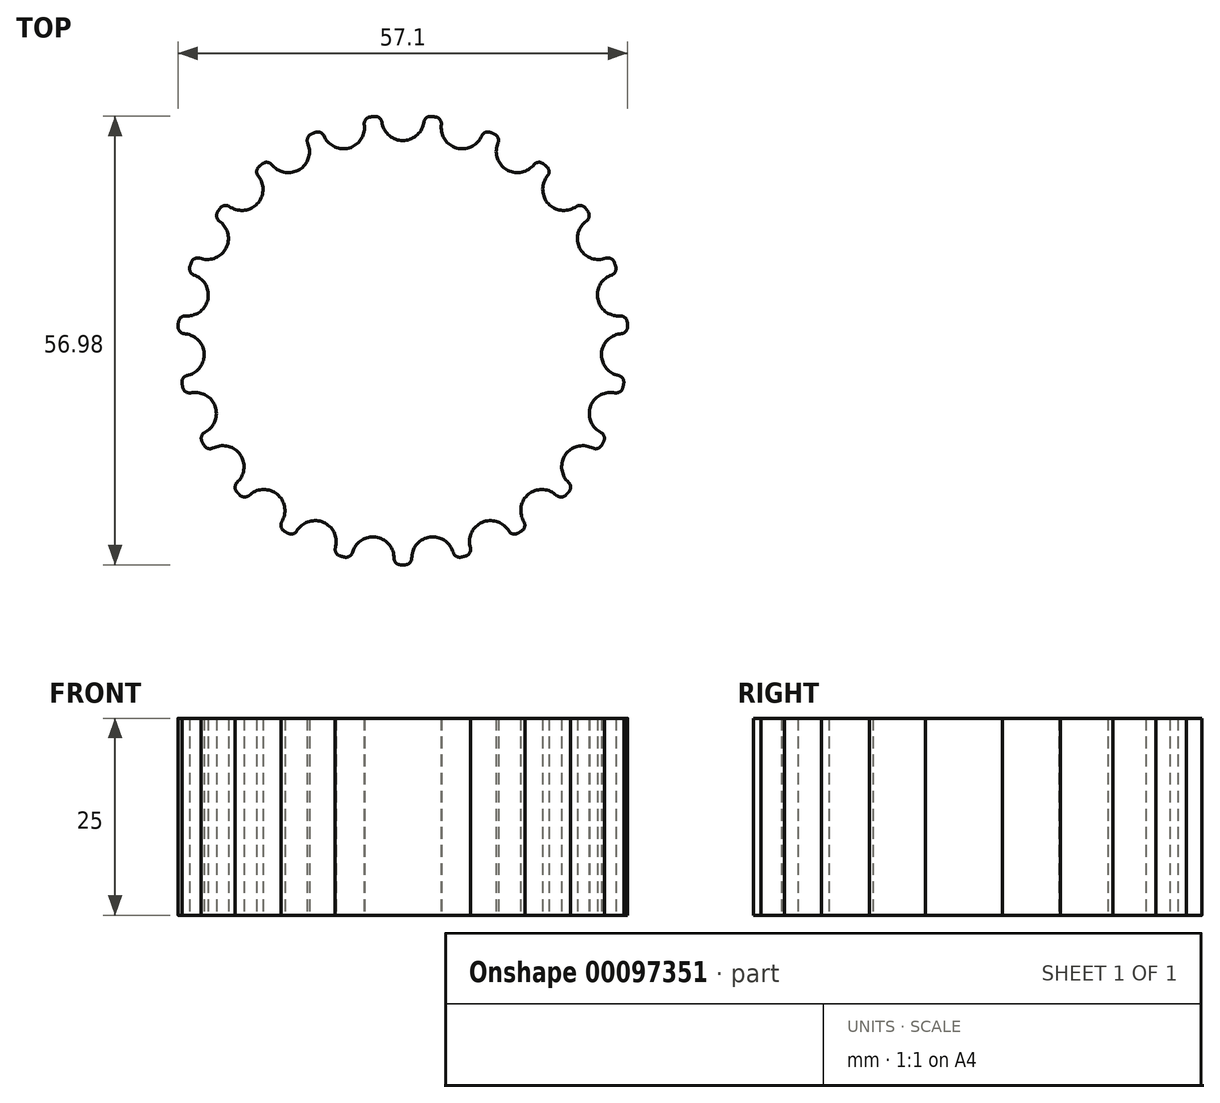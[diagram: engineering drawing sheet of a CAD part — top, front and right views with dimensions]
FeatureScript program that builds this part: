
annotation { "Feature Type Name" : "Feature", "Feature Type Description" : "" }
export const myFeature = defineFeature(function(context is Context, id is Id, definition is map)
    precondition{}
    {
        {
            var Q0;
            Q0=qCreatedBy(makeId("Top.planeOp"),FACE);
            var sketch = newSketch(context, id + "F0", { "sketchPlane" : qUnion([Q0])});
            skArc(sketch, "E0", {"start": v(-3.64, 28.37) * mm, "mid": v(-3.9, 28.33) * mm, "end": v(-4.15, 28.3) * mm});
            skCircle(sketch, "E1", {"center": v(0, 0) * mm, "radius": 25.3 * mm, "construction": true});
            skLineSegment(sketch, "E2", {"start": v(0, 0) * mm, "end": v(0, 27.98) * mm, "construction": true});
            skArc(sketch, "E3", {"start": v(-2.67, 27.67) * mm, "mid": v(-3.01, 28.21) * mm, "end": v(-3.64, 28.37) * mm});
            skArc(sketch, "E4", {"start": v(3.64, 28.37) * mm, "mid": v(3.01, 28.21) * mm, "end": v(2.67, 27.67) * mm});
            skArc(sketch, "E5", {"start": v(-2.62, 27.45) * mm, "mid": v(0, 25.3) * mm, "end": v(2.62, 27.45) * mm});
            skLineSegment(sketch, "E6", {"start": v(-2.67, 27.67) * mm, "end": v(-2.62, 27.45) * mm});
            skLineSegment(sketch, "E7", {"start": v(2.62, 27.45) * mm, "end": v(2.67, 27.67) * mm});
            skArc(sketch, "E8.1.0", {"start": v(-10.03, 25.93) * mm, "mid": v(-10.51, 26.35) * mm, "end": v(-11.15, 26.34) * mm});
            skArc(sketch, "E8.1.1", {"start": v(-4.15, 28.3) * mm, "mid": v(-4.7, 27.98) * mm, "end": v(-4.9, 27.37) * mm});
            skArc(sketch, "E8.1.2", {"start": v(-9.93, 25.73) * mm, "mid": v(-6.83, 24.36) * mm, "end": v(-4.88, 27.14) * mm});
            skLineSegment(sketch, "E8.1.3", {"start": v(-4.88, 27.14) * mm, "end": v(-4.9, 27.37) * mm});
            skLineSegment(sketch, "E8.1.4", {"start": v(-10.03, 25.93) * mm, "end": v(-9.93, 25.73) * mm});
            skArc(sketch, "E8.2.0", {"start": v(-16.66, 22.26) * mm, "mid": v(-17.23, 22.54) * mm, "end": v(-17.85, 22.35) * mm});
            skArc(sketch, "E8.2.1", {"start": v(-11.63, 26.13) * mm, "mid": v(-12.08, 25.67) * mm, "end": v(-12.1, 25.03) * mm});
            skArc(sketch, "E8.2.2", {"start": v(-16.5, 22.1) * mm, "mid": v(-13.15, 21.62) * mm, "end": v(-12.02, 24.82) * mm});
            skLineSegment(sketch, "E8.2.3", {"start": v(-12.02, 24.82) * mm, "end": v(-12.1, 25.03) * mm});
            skLineSegment(sketch, "E8.2.4", {"start": v(-16.66, 22.26) * mm, "end": v(-16.5, 22.1) * mm});
            skArc(sketch, "E8.3.0", {"start": v(-22.04, 16.94) * mm, "mid": v(-22.68, 17.05) * mm, "end": v(-23.21, 16.7) * mm});
            skArc(sketch, "E8.3.1", {"start": v(-18.25, 22.02) * mm, "mid": v(-18.56, 21.46) * mm, "end": v(-18.4, 20.84) * mm});
            skArc(sketch, "E8.3.2", {"start": v(-21.85, 16.82) * mm, "mid": v(-18.5, 17.27) * mm, "end": v(-18.27, 20.65) * mm});
            skLineSegment(sketch, "E8.3.3", {"start": v(-18.27, 20.65) * mm, "end": v(-18.4, 20.84) * mm});
            skLineSegment(sketch, "E8.3.4", {"start": v(-22.04, 16.94) * mm, "end": v(-21.85, 16.82) * mm});
            skArc(sketch, "E8.4.0", {"start": v(-25.8, 10.36) * mm, "mid": v(-26.43, 10.3) * mm, "end": v(-26.86, 9.82) * mm});
            skArc(sketch, "E8.4.1", {"start": v(-23.51, 16.28) * mm, "mid": v(-23.66, 15.66) * mm, "end": v(-23.34, 15.1) * mm});
            skArc(sketch, "E8.4.2", {"start": v(-25.58, 10.3) * mm, "mid": v(-22.46, 11.64) * mm, "end": v(-23.17, 14.96) * mm});
            skLineSegment(sketch, "E8.4.3", {"start": v(-23.17, 14.96) * mm, "end": v(-23.34, 15.1) * mm});
            skLineSegment(sketch, "E8.4.4", {"start": v(-25.8, 10.36) * mm, "end": v(-25.58, 10.3) * mm});
            skArc(sketch, "E8.5.0", {"start": v(-27.64, 3.02) * mm, "mid": v(-28.23, 2.79) * mm, "end": v(-28.51, 2.21) * mm});
            skArc(sketch, "E8.5.1", {"start": v(-27.03, 9.33) * mm, "mid": v(-27, 8.7) * mm, "end": v(-26.55, 8.24) * mm});
            skArc(sketch, "E8.5.2", {"start": v(-27.41, 3.02) * mm, "mid": v(-24.77, 5.15) * mm, "end": v(-26.34, 8.15) * mm});
            skLineSegment(sketch, "E8.5.3", {"start": v(-26.34, 8.15) * mm, "end": v(-26.55, 8.24) * mm});
            skLineSegment(sketch, "E8.5.4", {"start": v(-27.64, 3.02) * mm, "end": v(-27.41, 3.02) * mm});
            skArc(sketch, "E8.6.0", {"start": v(-27.43, -4.55) * mm, "mid": v(-27.94, -4.93) * mm, "end": v(-28.05, -5.56) * mm});
            skArc(sketch, "E8.6.1", {"start": v(-28.55, 1.7) * mm, "mid": v(-28.35, 1.08) * mm, "end": v(-27.79, 0.77) * mm});
            skArc(sketch, "E8.6.2", {"start": v(-27.2, -4.5) * mm, "mid": v(-25.24, -1.73) * mm, "end": v(-27.57, 0.74) * mm});
            skLineSegment(sketch, "E8.6.3", {"start": v(-27.57, 0.74) * mm, "end": v(-27.79, 0.77) * mm});
            skLineSegment(sketch, "E8.6.4", {"start": v(-27.43, -4.55) * mm, "end": v(-27.2, -4.5) * mm});
            skArc(sketch, "E8.7.0", {"start": v(-25.18, -11.78) * mm, "mid": v(-25.57, -12.29) * mm, "end": v(-25.51, -12.93) * mm});
            skArc(sketch, "E8.7.1", {"start": v(-27.95, -6.07) * mm, "mid": v(-27.6, -6.6) * mm, "end": v(-26.97, -6.75) * mm});
            skArc(sketch, "E8.7.2", {"start": v(-24.99, -11.66) * mm, "mid": v(-23.84, -8.47) * mm, "end": v(-26.74, -6.72) * mm});
            skLineSegment(sketch, "E8.7.3", {"start": v(-26.74, -6.72) * mm, "end": v(-26.97, -6.75) * mm});
            skLineSegment(sketch, "E8.7.4", {"start": v(-25.18, -11.78) * mm, "end": v(-24.99, -11.66) * mm});
            skArc(sketch, "E8.8.0", {"start": v(-21.07, -18.14) * mm, "mid": v(-21.3, -18.73) * mm, "end": v(-21.08, -19.33) * mm});
            skArc(sketch, "E8.8.1", {"start": v(-25.27, -13.39) * mm, "mid": v(-24.79, -13.8) * mm, "end": v(-24.15, -13.78) * mm});
            skArc(sketch, "E8.8.2", {"start": v(-20.91, -17.97) * mm, "mid": v(-20.67, -14.6) * mm, "end": v(-23.94, -13.69) * mm});
            skLineSegment(sketch, "E8.8.3", {"start": v(-23.94, -13.69) * mm, "end": v(-24.15, -13.78) * mm});
            skLineSegment(sketch, "E8.8.4", {"start": v(-21.07, -18.14) * mm, "end": v(-20.91, -17.97) * mm});
            skArc(sketch, "E8.9.0", {"start": v(-15.4, -23.15) * mm, "mid": v(-15.47, -23.79) * mm, "end": v(-15.08, -24.3) * mm});
            skArc(sketch, "E8.9.1", {"start": v(-20.72, -19.71) * mm, "mid": v(-20.14, -19.98) * mm, "end": v(-19.53, -19.78) * mm});
            skArc(sketch, "E8.9.2", {"start": v(-15.29, -22.95) * mm, "mid": v(-15.97, -19.63) * mm, "end": v(-19.36, -19.64) * mm});
            skLineSegment(sketch, "E8.9.3", {"start": v(-19.36, -19.64) * mm, "end": v(-19.53, -19.78) * mm});
            skLineSegment(sketch, "E8.9.4", {"start": v(-15.4, -23.15) * mm, "end": v(-15.29, -22.95) * mm});
            skArc(sketch, "E8.10.0", {"start": v(-8.58, -26.44) * mm, "mid": v(-8.47, -27.08) * mm, "end": v(-7.97, -27.47) * mm});
            skArc(sketch, "E8.10.1", {"start": v(-14.64, -24.57) * mm, "mid": v(-14, -24.67) * mm, "end": v(-13.47, -24.32) * mm});
            skArc(sketch, "E8.10.2", {"start": v(-8.53, -26.22) * mm, "mid": v(-10.08, -23.2) * mm, "end": v(-13.34, -24.13) * mm});
            skLineSegment(sketch, "E8.10.3", {"start": v(-13.34, -24.13) * mm, "end": v(-13.47, -24.32) * mm});
            skLineSegment(sketch, "E8.10.4", {"start": v(-8.58, -26.44) * mm, "end": v(-8.53, -26.22) * mm});
            skArc(sketch, "E8.11.0", {"start": v(-1.13, -27.78) * mm, "mid": v(-0.85, -28.36) * mm, "end": v(-0.26, -28.6) * mm});
            skArc(sketch, "E8.11.1", {"start": v(-7.46, -27.6) * mm, "mid": v(-6.83, -27.54) * mm, "end": v(-6.41, -27.05) * mm});
            skArc(sketch, "E8.11.2", {"start": v(-1.14, -27.55) * mm, "mid": v(-3.45, -25.06) * mm, "end": v(-6.34, -26.84) * mm});
            skLineSegment(sketch, "E8.11.3", {"start": v(-6.34, -26.84) * mm, "end": v(-6.41, -27.05) * mm});
            skLineSegment(sketch, "E8.11.4", {"start": v(-1.13, -27.78) * mm, "end": v(-1.14, -27.55) * mm});
            skArc(sketch, "E8.12.0", {"start": v(6.41, -27.05) * mm, "mid": v(6.83, -27.54) * mm, "end": v(7.46, -27.6) * mm});
            skArc(sketch, "E8.12.1", {"start": v(0.26, -28.6) * mm, "mid": v(0.85, -28.36) * mm, "end": v(1.13, -27.78) * mm});
            skArc(sketch, "E8.12.2", {"start": v(6.34, -26.84) * mm, "mid": v(3.45, -25.06) * mm, "end": v(1.14, -27.55) * mm});
            skLineSegment(sketch, "E8.12.3", {"start": v(1.14, -27.55) * mm, "end": v(1.13, -27.78) * mm});
            skLineSegment(sketch, "E8.12.4", {"start": v(6.41, -27.05) * mm, "end": v(6.34, -26.84) * mm});
            skArc(sketch, "E8.13.0", {"start": v(13.47, -24.32) * mm, "mid": v(14, -24.67) * mm, "end": v(14.64, -24.57) * mm});
            skArc(sketch, "E8.13.1", {"start": v(7.97, -27.47) * mm, "mid": v(8.47, -27.08) * mm, "end": v(8.58, -26.44) * mm});
            skArc(sketch, "E8.13.2", {"start": v(13.34, -24.13) * mm, "mid": v(10.08, -23.2) * mm, "end": v(8.53, -26.22) * mm});
            skLineSegment(sketch, "E8.13.3", {"start": v(8.53, -26.22) * mm, "end": v(8.58, -26.44) * mm});
            skLineSegment(sketch, "E8.13.4", {"start": v(13.47, -24.32) * mm, "end": v(13.34, -24.13) * mm});
            skArc(sketch, "E8.14.0", {"start": v(19.53, -19.78) * mm, "mid": v(20.14, -19.98) * mm, "end": v(20.72, -19.71) * mm});
            skArc(sketch, "E8.14.1", {"start": v(15.08, -24.3) * mm, "mid": v(15.47, -23.79) * mm, "end": v(15.4, -23.15) * mm});
            skArc(sketch, "E8.14.2", {"start": v(19.36, -19.64) * mm, "mid": v(15.97, -19.63) * mm, "end": v(15.29, -22.95) * mm});
            skLineSegment(sketch, "E8.14.3", {"start": v(15.29, -22.95) * mm, "end": v(15.4, -23.15) * mm});
            skLineSegment(sketch, "E8.14.4", {"start": v(19.53, -19.78) * mm, "end": v(19.36, -19.64) * mm});
            skArc(sketch, "E8.15.0", {"start": v(24.15, -13.78) * mm, "mid": v(24.79, -13.8) * mm, "end": v(25.27, -13.39) * mm});
            skArc(sketch, "E8.15.1", {"start": v(21.08, -19.33) * mm, "mid": v(21.3, -18.73) * mm, "end": v(21.07, -18.14) * mm});
            skArc(sketch, "E8.15.2", {"start": v(23.94, -13.69) * mm, "mid": v(20.67, -14.6) * mm, "end": v(20.91, -17.97) * mm});
            skLineSegment(sketch, "E8.15.3", {"start": v(20.91, -17.97) * mm, "end": v(21.07, -18.14) * mm});
            skLineSegment(sketch, "E8.15.4", {"start": v(24.15, -13.78) * mm, "end": v(23.94, -13.69) * mm});
            skArc(sketch, "E8.16.0", {"start": v(26.97, -6.75) * mm, "mid": v(27.6, -6.6) * mm, "end": v(27.95, -6.07) * mm});
            skArc(sketch, "E8.16.1", {"start": v(25.51, -12.93) * mm, "mid": v(25.57, -12.29) * mm, "end": v(25.18, -11.78) * mm});
            skArc(sketch, "E8.16.2", {"start": v(26.74, -6.72) * mm, "mid": v(23.84, -8.47) * mm, "end": v(24.99, -11.66) * mm});
            skLineSegment(sketch, "E8.16.3", {"start": v(24.99, -11.66) * mm, "end": v(25.18, -11.78) * mm});
            skLineSegment(sketch, "E8.16.4", {"start": v(26.97, -6.75) * mm, "end": v(26.74, -6.72) * mm});
            skArc(sketch, "E8.17.0", {"start": v(27.79, 0.77) * mm, "mid": v(28.35, 1.08) * mm, "end": v(28.55, 1.7) * mm});
            skArc(sketch, "E8.17.1", {"start": v(28.05, -5.56) * mm, "mid": v(27.94, -4.93) * mm, "end": v(27.43, -4.55) * mm});
            skArc(sketch, "E8.17.2", {"start": v(27.57, 0.74) * mm, "mid": v(25.24, -1.73) * mm, "end": v(27.2, -4.5) * mm});
            skLineSegment(sketch, "E8.17.3", {"start": v(27.2, -4.5) * mm, "end": v(27.43, -4.55) * mm});
            skLineSegment(sketch, "E8.17.4", {"start": v(27.79, 0.77) * mm, "end": v(27.57, 0.74) * mm});
            skArc(sketch, "E8.18.0", {"start": v(26.55, 8.24) * mm, "mid": v(27, 8.7) * mm, "end": v(27.03, 9.33) * mm});
            skArc(sketch, "E8.18.1", {"start": v(28.51, 2.21) * mm, "mid": v(28.23, 2.79) * mm, "end": v(27.64, 3.02) * mm});
            skArc(sketch, "E8.18.2", {"start": v(26.34, 8.15) * mm, "mid": v(24.77, 5.15) * mm, "end": v(27.41, 3.02) * mm});
            skLineSegment(sketch, "E8.18.3", {"start": v(27.41, 3.02) * mm, "end": v(27.64, 3.02) * mm});
            skLineSegment(sketch, "E8.18.4", {"start": v(26.55, 8.24) * mm, "end": v(26.34, 8.15) * mm});
            skArc(sketch, "E8.19.0", {"start": v(23.34, 15.1) * mm, "mid": v(23.66, 15.66) * mm, "end": v(23.51, 16.28) * mm});
            skArc(sketch, "E8.19.1", {"start": v(26.86, 9.82) * mm, "mid": v(26.43, 10.3) * mm, "end": v(25.8, 10.36) * mm});
            skArc(sketch, "E8.19.2", {"start": v(23.17, 14.96) * mm, "mid": v(22.46, 11.64) * mm, "end": v(25.58, 10.3) * mm});
            skLineSegment(sketch, "E8.19.3", {"start": v(25.58, 10.3) * mm, "end": v(25.8, 10.36) * mm});
            skLineSegment(sketch, "E8.19.4", {"start": v(23.34, 15.1) * mm, "end": v(23.17, 14.96) * mm});
            skArc(sketch, "E8.20.0", {"start": v(18.4, 20.84) * mm, "mid": v(18.56, 21.46) * mm, "end": v(18.25, 22.02) * mm});
            skArc(sketch, "E8.20.1", {"start": v(23.21, 16.7) * mm, "mid": v(22.68, 17.05) * mm, "end": v(22.04, 16.94) * mm});
            skArc(sketch, "E8.20.2", {"start": v(18.27, 20.65) * mm, "mid": v(18.5, 17.27) * mm, "end": v(21.85, 16.82) * mm});
            skLineSegment(sketch, "E8.20.3", {"start": v(21.85, 16.82) * mm, "end": v(22.04, 16.94) * mm});
            skLineSegment(sketch, "E8.20.4", {"start": v(18.4, 20.84) * mm, "end": v(18.27, 20.65) * mm});
            skArc(sketch, "E8.21.0", {"start": v(12.1, 25.03) * mm, "mid": v(12.08, 25.67) * mm, "end": v(11.63, 26.13) * mm});
            skArc(sketch, "E8.21.1", {"start": v(17.85, 22.35) * mm, "mid": v(17.23, 22.54) * mm, "end": v(16.66, 22.26) * mm});
            skArc(sketch, "E8.21.2", {"start": v(12.02, 24.82) * mm, "mid": v(13.15, 21.62) * mm, "end": v(16.5, 22.1) * mm});
            skLineSegment(sketch, "E8.21.3", {"start": v(16.5, 22.1) * mm, "end": v(16.66, 22.26) * mm});
            skLineSegment(sketch, "E8.21.4", {"start": v(12.1, 25.03) * mm, "end": v(12.02, 24.82) * mm});
            skArc(sketch, "E8.22.0", {"start": v(4.9, 27.37) * mm, "mid": v(4.7, 27.98) * mm, "end": v(4.15, 28.3) * mm});
            skArc(sketch, "E8.22.1", {"start": v(11.15, 26.34) * mm, "mid": v(10.51, 26.35) * mm, "end": v(10.03, 25.93) * mm});
            skArc(sketch, "E8.22.2", {"start": v(4.88, 27.14) * mm, "mid": v(6.83, 24.36) * mm, "end": v(9.93, 25.73) * mm});
            skLineSegment(sketch, "E8.22.3", {"start": v(9.93, 25.73) * mm, "end": v(10.03, 25.93) * mm});
            skLineSegment(sketch, "E8.22.4", {"start": v(4.9, 27.37) * mm, "end": v(4.88, 27.14) * mm});
            skArc(sketch, "E9.trimOffspring", {"start": v(4.15, 28.3) * mm, "mid": v(3.9, 28.33) * mm, "end": v(3.64, 28.37) * mm});
            skArc(sketch, "E10.trimOffspring", {"start": v(11.63, 26.13) * mm, "mid": v(11.4, 26.23) * mm, "end": v(11.15, 26.34) * mm});
            skArc(sketch, "E11.trimOffspring", {"start": v(18.25, 22.02) * mm, "mid": v(18.05, 22.19) * mm, "end": v(17.85, 22.35) * mm});
            skArc(sketch, "E12.trimOffspring", {"start": v(-11.15, 26.34) * mm, "mid": v(-11.4, 26.23) * mm, "end": v(-11.63, 26.13) * mm});
            skArc(sketch, "E13.trimOffspring", {"start": v(23.51, 16.28) * mm, "mid": v(23.37, 16.5) * mm, "end": v(23.21, 16.7) * mm});
            skArc(sketch, "E14.trimOffspring", {"start": v(27.03, 9.33) * mm, "mid": v(26.95, 9.58) * mm, "end": v(26.86, 9.82) * mm});
            skArc(sketch, "E15.trimOffspring", {"start": v(28.55, 1.7) * mm, "mid": v(28.53, 1.95) * mm, "end": v(28.51, 2.21) * mm});
            skArc(sketch, "E16.trimOffspring", {"start": v(27.95, -6.07) * mm, "mid": v(28, -5.82) * mm, "end": v(28.05, -5.56) * mm});
            skArc(sketch, "E17.trimOffspring", {"start": v(25.27, -13.39) * mm, "mid": v(25.4, -13.16) * mm, "end": v(25.51, -12.93) * mm});
            skArc(sketch, "E18.trimOffspring", {"start": v(20.72, -19.71) * mm, "mid": v(20.9, -19.52) * mm, "end": v(21.08, -19.33) * mm});
            skArc(sketch, "E19.trimOffspring", {"start": v(-17.85, 22.35) * mm, "mid": v(-18.05, 22.19) * mm, "end": v(-18.25, 22.02) * mm});
            skArc(sketch, "E20.trimOffspring", {"start": v(-23.21, 16.7) * mm, "mid": v(-23.37, 16.5) * mm, "end": v(-23.51, 16.28) * mm});
            skArc(sketch, "E21.trimOffspring", {"start": v(-28.51, 2.21) * mm, "mid": v(-28.53, 1.95) * mm, "end": v(-28.55, 1.7) * mm});
            skArc(sketch, "E22.trimOffspring", {"start": v(-28.05, -5.56) * mm, "mid": v(-28, -5.82) * mm, "end": v(-27.95, -6.07) * mm});
            skArc(sketch, "E23.trimOffspring", {"start": v(-25.51, -12.93) * mm, "mid": v(-25.4, -13.16) * mm, "end": v(-25.27, -13.39) * mm});
            skArc(sketch, "E24.trimOffspring", {"start": v(-21.08, -19.33) * mm, "mid": v(-20.9, -19.52) * mm, "end": v(-20.72, -19.71) * mm});
            skArc(sketch, "E25.trimOffspring", {"start": v(-15.08, -24.3) * mm, "mid": v(-14.86, -24.44) * mm, "end": v(-14.64, -24.57) * mm});
            skArc(sketch, "E26.trimOffspring", {"start": v(-7.97, -27.47) * mm, "mid": v(-7.72, -27.54) * mm, "end": v(-7.46, -27.6) * mm});
            skArc(sketch, "E27.trimOffspring", {"start": v(-0.26, -28.6) * mm, "mid": v(0, -28.6) * mm, "end": v(0.26, -28.6) * mm});
            skArc(sketch, "E28.trimOffspring", {"start": v(7.46, -27.6) * mm, "mid": v(7.72, -27.54) * mm, "end": v(7.97, -27.47) * mm});
            skArc(sketch, "E29.trimOffspring", {"start": v(14.64, -24.57) * mm, "mid": v(14.86, -24.44) * mm, "end": v(15.08, -24.3) * mm});
            skArc(sketch, "E30.trimOffspring", {"start": v(-26.86, 9.82) * mm, "mid": v(-26.95, 9.58) * mm, "end": v(-27.03, 9.33) * mm});
            skSolve(sketch);
        }
        {
            var Q0;
            Q0 = qSketchRegion(id + "F0", true);
            extrude(context, id + "F1", {"entities" : qUnion([Q0]), "depth" : 25 * mm});
        }
    });
